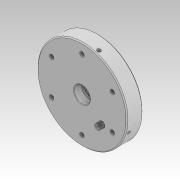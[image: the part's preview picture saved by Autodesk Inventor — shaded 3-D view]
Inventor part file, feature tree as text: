
AUTODESK INVENTOR PART (.ipt)
format: ipt  version: 2020 (Build 240168000, 168)  size: 809,472 bytes
history: native  units: mm
features: sketch x13, extrude x11, plane x3, pattern_circular x2, chamfer x2, fillet x2, revolve x1, projected_geometry x1
ambient origin geometry x8: Origin, YZ Plane, XZ Plane, XY Plane, X Axis, Y Axis, Z Axis, Center Point
bodies: Solid1 (feature_tree)
feature tree (35):
  extrude  "Extrusion1"  Depth=90.0mm
  extrude  "Extrusion6"  TaperAngle=0.0deg  [1 undecoded]
  extrude  "Extrusion5"  Depth=16.0mm TaperAngle=0.0deg
  pattern_circular  "Circular Pattern2"  Count=6 Angle=360.0deg
  extrude  "Extrusion7"  Depth=5.6mm
  extrude  "Extrusion8"  Depth=4.0mm TaperAngle=360.0deg
  pattern_circular  "Circular Pattern1"  [2 undecoded]
  extrude  "Extrusion11"  Depth=3.0mm
  extrude  "Extrusion12"  Depth=1.0mm TaperAngle=0.0deg
  extrude  "Extrusion13"  TaperAngle=90.0deg  [1 undecoded]
  plane  "Work Plane1"
  sketch  "Sketch13"  dims[d44=3.0mm]
  plane  "Work Plane2"
  plane  "Work Plane3"
  extrude  "Extrusion14"  Depth=1.0mm
  extrude  "Extrusion15"  Depth=1.0mm
  chamfer  "Chamfer1"  Distance=1.0mm Angle=45.0deg
  fillet  "Fillet1"  [1 undecoded]
  revolve  "Revolution1"  [1 undecoded]
  fillet  "Fillet2"  Radius=0.75mm
  chamfer  "Chamfer2"  Distance=200.0mm Angle=360.0deg
  extrude  "Extrusion16"  Depth=1.0mm
  sketch  "Sketch1"  dims[d0=12.6mm d1=90.0mm]
  sketch  "Sketch4"  dims[d2=16.0mm d3=0.0mm d20=0.0mm d21=0.0mm]
  sketch  "Sketch5"  dims[d22=16.0mm d23=7.5mm d24=0.0mm]
  sketch  "Sketch6"  dims[d25=3.5mm]
  sketch  "Sketch7"  dims[d26=35.0mm d27=60.0mm d29=360.0deg]
  sketch  "Sketch10"  dims[d31=0.0mm d32=0.0mm d33=5.6mm]
  sketch  "Sketch11"  dims[d34=4.0mm d35=0.0mm d40=60.0mm d41=360.0deg]
  sketch  "Sketch12"  dims[d43=25.0mm]
  sketch  "Sketch14"  dims[d45=7.0mm d46=0.0mm]
  sketch  "Sketch15"  dims[d47=4.0mm d48=0.0mm]
  projected_geometry  "Projected Loop1"
  sketch  "Sketch16"  dims[d50=4.0mm d51=0.0mm]
  sketch  "Sketch17"  dims[d52=3.5mm d53=7.5mm d54=0.0mm d55=3.0mm d56=7.5mm d57=0.0mm d58=90.0deg d59=50.0mm d60=2.96706mm d61=1.0mm d62=2.0mm d63=45.0deg d64=45.0deg d65=2.0mm d66=0.75mm d67=10.9mm d68=12.6mm d69=200.0mm d70=360.0deg d72=1.308997mm d73=5.0mm d75=6.0mm d76=2.5mm d77=30.0deg d78=3.0mm d79=90.0deg d80=0.3mm d81=0.5mm d82=2.0mm d83=45.0deg d84=59.0mm d85=86.0mm d86=1.0mm d87=0.0mm]
note: 6 required parameter values undecoded (feature->parameter linkage not recoverable at this tier; creation-order binding heuristic only, values carry confidence <= 0.55)